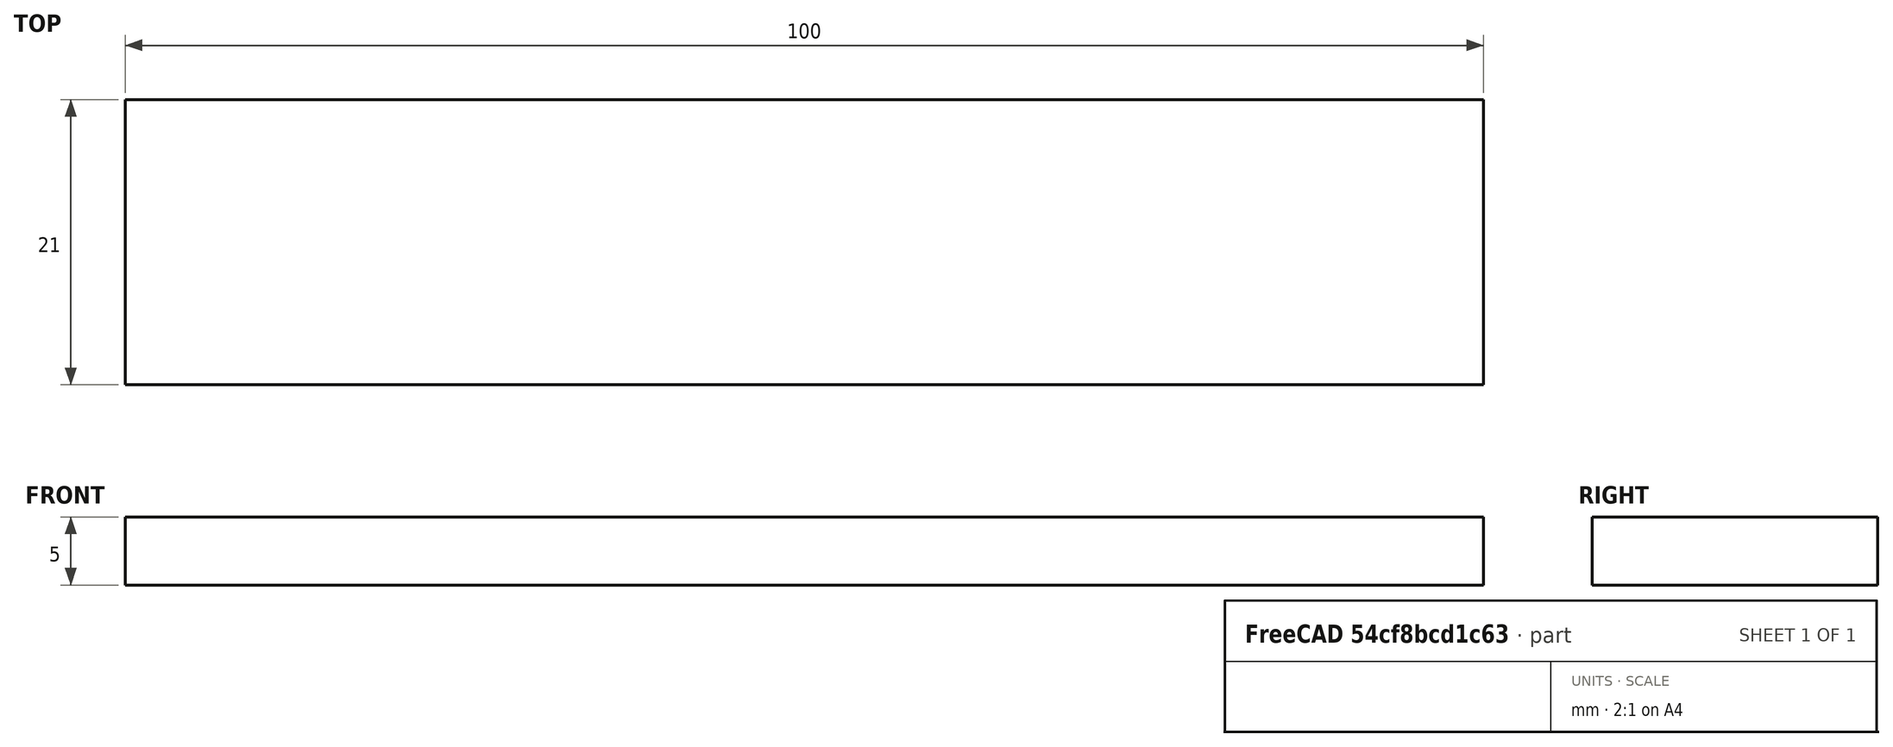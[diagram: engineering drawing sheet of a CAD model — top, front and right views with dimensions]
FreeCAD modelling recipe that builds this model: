
FCSTD DOCUMENT  (FreeCAD 0.19R24267 +99 (Git))
Label: Sample object
License: All rights reserved
LicenseURL: http://en.wikipedia.org/wiki/All_rights_reserved
objects: Sketcher::SketchObject×1, PartDesign::Pad×1, PartDesign::Body×1
note: 4 computed .brp shape members not serialized (recipe doc carries the construction recipe); baked Part::Feature solids carry a one-line shape summary decoded from their .brp

FEATURE [Sketcher::SketchObject] Sketch
  FullyConstrained = true
  MapMode = 5
  Support = -> [XY_Plane]
  sketch-geometry (4):
    g0: LineSegment StartX=0 StartY=0 StartZ=0 EndX=100 EndY=0 EndZ=0
    g1: LineSegment StartX=100 StartY=0 StartZ=0 EndX=100 EndY=21 EndZ=0
    g2: LineSegment StartX=100 StartY=21 StartZ=0 EndX=0 EndY=21 EndZ=0
    g3: LineSegment StartX=0 StartY=21 StartZ=0 EndX=0 EndY=0 EndZ=0
  constraints (11):
    c: Coincident(g0,g1)
    c: Coincident(g1,g2)
    c: Coincident(g2,g3)
    c: Coincident(g3,g0)
    c: Horizontal(g0)
    c: Horizontal(g2)
    c: Vertical(g1)
    c: Vertical(g3)
    c: Coincident(g0,g-1)
    c: DistanceY(g3,g3) = 21
    c: DistanceX(g2,g2) = 100
FEATURE [PartDesign::Pad] Pad
  Direction = (1,1,1)
  Length = 5
  Length2 = 100
  Profile = -> Sketch
  Type = 0
FEATURE [PartDesign::Body] Body
  Group = -> [Sketch,Pad]
  Origin = -> Origin
  Tip = -> Pad
